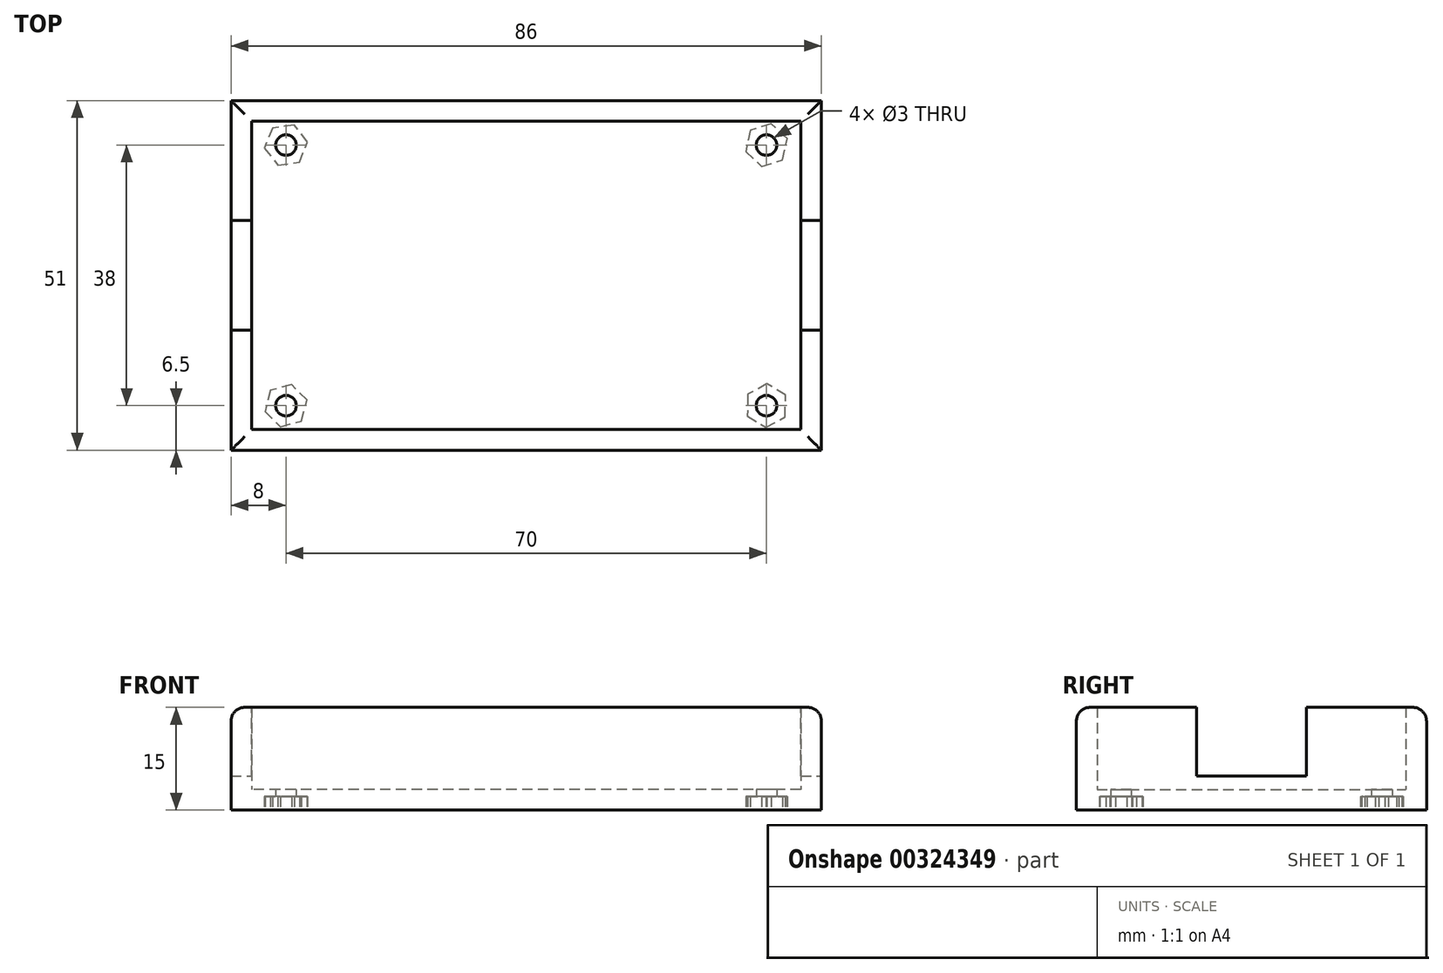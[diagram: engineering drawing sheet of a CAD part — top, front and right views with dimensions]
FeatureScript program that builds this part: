
annotation { "Feature Type Name" : "Feature", "Feature Type Description" : "" }
export const myFeature = defineFeature(function(context is Context, id is Id, definition is map)
    precondition{}
    {
        {
            var Q0;
            Q0=qCreatedBy(makeId("Top.planeOp"),FACE);
            var sketch = newSketch(context, id + "F0", { "sketchPlane" : qUnion([Q0])});
            skLineSegment(sketch, "E0.bottom", {"start": v(-40, 22.5) * mm, "end": v(40, 22.5) * mm});
            skLineSegment(sketch, "E0.top", {"start": v(-40, -22.5) * mm, "end": v(40, -22.5) * mm});
            skLineSegment(sketch, "E0.left", {"start": v(-40, 22.5) * mm, "end": v(-40, -22.5) * mm});
            skLineSegment(sketch, "E0.right", {"start": v(40, 22.5) * mm, "end": v(40, -22.5) * mm});
            skLineSegment(sketch, "E1.0", {"start": v(-43, 25.5) * mm, "end": v(43, 25.5) * mm});
            skLineSegment(sketch, "E1.1", {"start": v(-43, 25.5) * mm, "end": v(-43, -25.5) * mm});
            skLineSegment(sketch, "E1.2", {"start": v(-43, -25.5) * mm, "end": v(43, -25.5) * mm});
            skLineSegment(sketch, "E1.3", {"start": v(43, 25.5) * mm, "end": v(43, -25.5) * mm});
            skCircle(sketch, "E2", {"center": v(-35, 19) * mm, "radius": 1.5 * mm});
            skCircle(sketch, "E3", {"center": v(-35, -19) * mm, "radius": 1.5 * mm});
            skCircle(sketch, "E4", {"center": v(35, -19) * mm, "radius": 1.5 * mm});
            skCircle(sketch, "E5", {"center": v(35, 19) * mm, "radius": 1.5 * mm});
            skSolve(sketch);
        }
        {
            var Q0;
            Q0=makeQuery(id+"F0.imprint","IMPRINT",FACE,{"disambiguationData":[TD([[makeQuery(id+"F0.imprint","IMPRINT",EDGE,{"derivedFrom":sQuery(id+"F0.wireOp",EDGE,"E0.bottom")}),-1.0]])]});
            var Q1;
            Q1=makeQuery(id+"F0.imprint","IMPRINT",FACE,{"disambiguationData":[TD([[makeQuery(id+"F0.imprint","IMPRINT",EDGE,{"derivedFrom":sQuery(id+"F0.wireOp",EDGE,"E0.bottom")}),1.0]])]});
            extrude(context, id + "F1", {"entities" : qUnion([Q0, Q1]), "depth" : 3 * mm});
        }
        {
            var Q0;
            Q0=makeQuery(id+"F0.imprint","IMPRINT",FACE,{"disambiguationData":[TD([[makeQuery(id+"F0.imprint","IMPRINT",EDGE,{"derivedFrom":sQuery(id+"F0.wireOp",EDGE,"E0.bottom")}),1.0]])]});
            extrude(context, id + "F2", {"entities" : qUnion([Q0]), "operationType" : NewBodyOperationType.ADD, "depth" : 15 * mm});
        }
        {
            var Q0;
            Q0=makeQuery(id+"F2.opExtrude","CAP_FACE",FACE,{"disambiguationData":[OSD([sQuery(id+"F0.wireOp",EDGE,"E0.bottom"),sQuery(id+"F0.wireOp",EDGE,"E0.top"),sQuery(id+"F0.wireOp",EDGE,"E0.left"),sQuery(id+"F0.wireOp",EDGE,"E0.right"),sQuery(id+"F0.wireOp",EDGE,"E1.0"),sQuery(id+"F0.wireOp",EDGE,"E1.1"),sQuery(id+"F0.wireOp",EDGE,"E1.2"),sQuery(id+"F0.wireOp",EDGE,"E1.3")])],"isStart":false});
            var sketch = newSketch(context, id + "F3", { "sketchPlane" : qUnion([Q0])});
            skLineSegment(sketch, "E6.bottom", {"start": v(-43, 8) * mm, "end": v(-40, 8) * mm});
            skLineSegment(sketch, "E6.top", {"start": v(-43, -8) * mm, "end": v(-40, -8) * mm});
            skLineSegment(sketch, "E6.left", {"start": v(-43, 8) * mm, "end": v(-43, -8) * mm});
            skLineSegment(sketch, "E6.right", {"start": v(-40, 8) * mm, "end": v(-40, -8) * mm});
            skLineSegment(sketch, "E7.bottom", {"start": v(40, 8) * mm, "end": v(43, 8) * mm});
            skLineSegment(sketch, "E7.top", {"start": v(40, -8) * mm, "end": v(43, -8) * mm});
            skLineSegment(sketch, "E7.left", {"start": v(40, 8) * mm, "end": v(40, -8) * mm});
            skLineSegment(sketch, "E7.right", {"start": v(43, 8) * mm, "end": v(43, -8) * mm});
            skSolve(sketch);
        }
        {
            var Q0;
            Q0=makeQuery(id+"F3.imprint","IMPRINT",FACE,{"disambiguationData":[TD([[makeQuery(id+"F3.imprint","IMPRINT",EDGE,{"derivedFrom":sQuery(id+"F3.wireOp",EDGE,"E6.bottom")}),-1.0]])]});
            var Q1;
            Q1=makeQuery(id+"F3.imprint","IMPRINT",FACE,{"disambiguationData":[TD([[makeQuery(id+"F3.imprint","IMPRINT",EDGE,{"derivedFrom":sQuery(id+"F3.wireOp",EDGE,"E7.bottom")}),-1.0]])]});
            extrude(context, id + "F4", {"entities" : qUnion([Q0, Q1]), "operationType" : NewBodyOperationType.REMOVE, "oppositeDirection" : true, "depth" : 10 * mm});
        }
        {
            var Q0;
            Q0=makeQuery(id+"F0.imprint","IMPRINT",FACE,{"disambiguationData":[TD([[makeQuery(id+"F0.imprint","IMPRINT",EDGE,{"derivedFrom":sQuery(id+"F0.wireOp",EDGE,"E0.bottom")}),1.0]])]});
            var sketch = newSketch(context, id + "F5", { "sketchPlane" : qUnion([Q0])});
            skLineSegment(sketch, "E8.bottom", {"start": v(43, 25.5) * mm, "end": v(33, 25.5) * mm});
            skLineSegment(sketch, "E8.top", {"start": v(43, 15.5) * mm, "end": v(40, 15.5) * mm});
            skLineSegment(sketch, "E8.left", {"start": v(43, 25.5) * mm, "end": v(43, 15.5) * mm});
            skLineSegment(sketch, "E8.right", {"start": v(33, 25.5) * mm, "end": v(33, 22.5) * mm});
            skLineSegment(sketch, "E9.top", {"start": v(40, 22.5) * mm, "end": v(33, 22.5) * mm});
            skLineSegment(sketch, "E9.left", {"start": v(40, 15.5) * mm, "end": v(40, 22.5) * mm});
            skLineSegment(sketch, "E10.MirrorCS", {"start": v(-33, 25.5) * mm, "end": v(-33, 22.5) * mm});
            skLineSegment(sketch, "E11.MirrorCS", {"start": v(-40, 22.5) * mm, "end": v(-33, 22.5) * mm});
            skLineSegment(sketch, "E12.MirrorCS", {"start": v(-40, 15.5) * mm, "end": v(-40, 22.5) * mm});
            skLineSegment(sketch, "E13.MirrorCS", {"start": v(-43, 15.5) * mm, "end": v(-40, 15.5) * mm});
            skLineSegment(sketch, "E14.MirrorCS", {"start": v(-43, 25.5) * mm, "end": v(-43, 15.5) * mm});
            skLineSegment(sketch, "E15.MirrorCS", {"start": v(-43, 25.5) * mm, "end": v(-33, 25.5) * mm});
            skLineSegment(sketch, "E16.MirrorCS", {"start": v(43, -15.5) * mm, "end": v(40, -15.5) * mm});
            skLineSegment(sketch, "E17.MirrorCS", {"start": v(43, -25.5) * mm, "end": v(43, -15.5) * mm});
            skLineSegment(sketch, "E18.MirrorCS", {"start": v(40, -15.5) * mm, "end": v(40, -22.5) * mm});
            skLineSegment(sketch, "E19.MirrorCS", {"start": v(40, -22.5) * mm, "end": v(33, -22.5) * mm});
            skLineSegment(sketch, "E20.MirrorCS", {"start": v(33, -25.5) * mm, "end": v(33, -22.5) * mm});
            skLineSegment(sketch, "E21.MirrorCS", {"start": v(43, -25.5) * mm, "end": v(33, -25.5) * mm});
            skLineSegment(sketch, "E22.MirrorCS", {"start": v(-40, -22.5) * mm, "end": v(-33, -22.5) * mm});
            skLineSegment(sketch, "E23.MirrorCS", {"start": v(-33, -25.5) * mm, "end": v(-33, -22.5) * mm});
            skLineSegment(sketch, "E24.MirrorCS", {"start": v(-43, -25.5) * mm, "end": v(-33, -25.5) * mm});
            skLineSegment(sketch, "E25.MirrorCS", {"start": v(-43, -25.5) * mm, "end": v(-43, -15.5) * mm});
            skLineSegment(sketch, "E26.MirrorCS", {"start": v(-43, -15.5) * mm, "end": v(-40, -15.5) * mm});
            skLineSegment(sketch, "E27.MirrorCS", {"start": v(-40, -15.5) * mm, "end": v(-40, -22.5) * mm});
            skSolve(sketch);
        }
        {
            var Q0;
            Q0=makeQuery(id+"F1.opExtrude","CAP_FACE",FACE,{"disambiguationData":[OSD([sQuery(id+"F0.wireOp",EDGE,"E1.0"),sQuery(id+"F0.wireOp",EDGE,"E1.1"),sQuery(id+"F0.wireOp",EDGE,"E1.2"),sQuery(id+"F0.wireOp",EDGE,"E1.3"),sQuery(id+"F0.wireOp",EDGE,"E2"),sQuery(id+"F0.wireOp",EDGE,"E3"),sQuery(id+"F0.wireOp",EDGE,"E4"),sQuery(id+"F0.wireOp",EDGE,"E5")])],"isStart":true});
            var sketch = newSketch(context, id + "F6", { "sketchPlane" : qUnion([Q0])});
            skCircle(sketch, "E28.cCircle", {"center": v(-35, 19) * mm, "radius": 2.75 * mm, "construction": true});
            skLineSegment(sketch, "E28.0", {"start": v(-31.94, 18.16) * mm, "end": v(-34.2, 15.93) * mm});
            skLineSegment(sketch, "E28.1", {"start": v(-34.2, 15.93) * mm, "end": v(-37.26, 16.77) * mm});
            skLineSegment(sketch, "E28.2", {"start": v(-37.26, 16.77) * mm, "end": v(-38.06, 19.84) * mm});
            skLineSegment(sketch, "E28.3", {"start": v(-38.06, 19.84) * mm, "end": v(-35.8, 22.07) * mm});
            skLineSegment(sketch, "E28.4", {"start": v(-35.8, 22.07) * mm, "end": v(-32.74, 21.23) * mm});
            skLineSegment(sketch, "E28.5", {"start": v(-32.74, 21.23) * mm, "end": v(-31.94, 18.16) * mm});
            skPoint(sketch, "E28.0.midPoint", {"position": v(-33.07, 17.05) * mm});
            skCircle(sketch, "E29.cCircle", {"center": v(35, 19) * mm, "radius": 2.75 * mm, "construction": true});
            skLineSegment(sketch, "E29.0", {"start": v(37.78, 17.47) * mm, "end": v(35.07, 15.83) * mm});
            skLineSegment(sketch, "E29.1", {"start": v(35.07, 15.83) * mm, "end": v(32.29, 17.35) * mm});
            skLineSegment(sketch, "E29.2", {"start": v(32.29, 17.35) * mm, "end": v(32.22, 20.53) * mm});
            skLineSegment(sketch, "E29.3", {"start": v(32.22, 20.53) * mm, "end": v(34.93, 22.17) * mm});
            skLineSegment(sketch, "E29.4", {"start": v(34.93, 22.17) * mm, "end": v(37.71, 20.65) * mm});
            skLineSegment(sketch, "E29.5", {"start": v(37.71, 20.65) * mm, "end": v(37.78, 17.47) * mm});
            skPoint(sketch, "E29.0.midPoint", {"position": v(36.43, 16.65) * mm});
            skCircle(sketch, "E30.cCircle", {"center": v(-35, -19) * mm, "radius": 2.75 * mm, "construction": true});
            skLineSegment(sketch, "E30.0", {"start": v(-31.86, -19.44) * mm, "end": v(-33.81, -21.94) * mm});
            skLineSegment(sketch, "E30.1", {"start": v(-33.81, -21.94) * mm, "end": v(-36.96, -21.5) * mm});
            skLineSegment(sketch, "E30.2", {"start": v(-36.96, -21.5) * mm, "end": v(-38.14, -18.56) * mm});
            skLineSegment(sketch, "E30.3", {"start": v(-38.14, -18.56) * mm, "end": v(-36.19, -16.06) * mm});
            skLineSegment(sketch, "E30.4", {"start": v(-36.19, -16.06) * mm, "end": v(-33.04, -16.5) * mm});
            skLineSegment(sketch, "E30.5", {"start": v(-33.04, -16.5) * mm, "end": v(-31.86, -19.44) * mm});
            skPoint(sketch, "E30.0.midPoint", {"position": v(-32.83, -20.7) * mm});
            skCircle(sketch, "E31.cCircle", {"center": v(35, -19) * mm, "radius": 2.75 * mm, "construction": true});
            skLineSegment(sketch, "E31.0", {"start": v(38.03, -19.96) * mm, "end": v(35.68, -22.1) * mm});
            skLineSegment(sketch, "E31.1", {"start": v(35.68, -22.1) * mm, "end": v(32.65, -21.14) * mm});
            skLineSegment(sketch, "E31.2", {"start": v(32.65, -21.14) * mm, "end": v(31.97, -18.04) * mm});
            skLineSegment(sketch, "E31.3", {"start": v(31.97, -18.04) * mm, "end": v(34.32, -15.9) * mm});
            skLineSegment(sketch, "E31.4", {"start": v(34.32, -15.9) * mm, "end": v(37.35, -16.86) * mm});
            skLineSegment(sketch, "E31.5", {"start": v(37.35, -16.86) * mm, "end": v(38.03, -19.96) * mm});
            skPoint(sketch, "E31.0.midPoint", {"position": v(36.85, -21.03) * mm});
            skSolve(sketch);
        }
        {
            var Q0;
            Q0=makeQuery(id+"F6.imprint","IMPRINT",FACE,{"disambiguationData":[TD([[makeQuery(id+"F6.imprint","IMPRINT",EDGE,{"derivedFrom":sQuery(id+"F6.wireOp",EDGE,"E28.0")}),-1.0]])]});
            var Q1;
            Q1=makeQuery(id+"F6.imprint","IMPRINT",FACE,{"disambiguationData":[TD([[makeQuery(id+"F6.imprint","IMPRINT",EDGE,{"derivedFrom":sQuery(id+"F6.wireOp",EDGE,"E30.0")}),-1.0]])]});
            var Q2;
            Q2=makeQuery(id+"F6.imprint","IMPRINT",FACE,{"disambiguationData":[TD([[makeQuery(id+"F6.imprint","IMPRINT",EDGE,{"derivedFrom":sQuery(id+"F6.wireOp",EDGE,"E31.0")}),-1.0]])]});
            var Q3;
            Q3=makeQuery(id+"F6.imprint","IMPRINT",FACE,{"disambiguationData":[TD([[makeQuery(id+"F6.imprint","IMPRINT",EDGE,{"derivedFrom":sQuery(id+"F6.wireOp",EDGE,"E29.0")}),-1.0]])]});
            extrude(context, id + "F7", {"entities" : qUnion([Q0, Q1, Q2, Q3]), "operationType" : NewBodyOperationType.REMOVE, "oppositeDirection" : true, "depth" : 2 * mm});
        }
        {
            var Q0;
            Q0=makeQuery(id+"F2.opExtrude","CAP_EDGE",EDGE,{"disambiguationData":[OSD([sQuery(id+"F0.wireOp",EDGE,"E1.2")])],"isStart":false});
            var Q1;
            Q1=makeQuery(id+"F2.opExtrude","CAP_EDGE",EDGE,{"disambiguationData":[OSD([sQuery(id+"F0.wireOp",EDGE,"E1.0")])],"isStart":false});
            var Q2;
            {var subQ0=sQuery(id+"F0.wireOp",EDGE,"E1.0");var subQ1=sQuery(id+"F0.wireOp",EDGE,"E1.3");Q2=makeQuery(id+"F4.boolean.opBoolean","SPLIT",EDGE,{"disambiguationData":[TD([makeQuery(id+"F1.opExtrude","SWEPT_FACE",FACE,{"disambiguationData":[OSD([subQ0])]})])],"derivedFrom":makeQuery(id+"F2.opExtrude","CAP_EDGE",EDGE,{"disambiguationData":[OSD([subQ1])],"isStart":false})});}
            var Q3;
            {var subQ0=sQuery(id+"F0.wireOp",EDGE,"E1.3");var subQ1=sQuery(id+"F0.wireOp",EDGE,"E1.2");Q3=makeQuery(id+"F4.boolean.opBoolean","SPLIT",EDGE,{"disambiguationData":[TD([makeQuery(id+"F1.opExtrude","SWEPT_FACE",FACE,{"disambiguationData":[OSD([subQ1])]})])],"derivedFrom":makeQuery(id+"F2.opExtrude","CAP_EDGE",EDGE,{"disambiguationData":[OSD([subQ0])],"isStart":false})});}
            var Q4;
            {var subQ0=sQuery(id+"F0.wireOp",EDGE,"E1.0");var subQ1=sQuery(id+"F0.wireOp",EDGE,"E1.1");Q4=makeQuery(id+"F4.boolean.opBoolean","SPLIT",EDGE,{"disambiguationData":[TD([makeQuery(id+"F1.opExtrude","SWEPT_FACE",FACE,{"disambiguationData":[OSD([subQ0])]})])],"derivedFrom":makeQuery(id+"F2.opExtrude","CAP_EDGE",EDGE,{"disambiguationData":[OSD([subQ1])],"isStart":false})});}
            var Q5;
            {var subQ0=sQuery(id+"F0.wireOp",EDGE,"E1.2");var subQ1=sQuery(id+"F0.wireOp",EDGE,"E1.1");Q5=makeQuery(id+"F4.boolean.opBoolean","SPLIT",EDGE,{"disambiguationData":[TD([makeQuery(id+"F1.opExtrude","SWEPT_FACE",FACE,{"disambiguationData":[OSD([subQ0])]})])],"derivedFrom":makeQuery(id+"F2.opExtrude","CAP_EDGE",EDGE,{"disambiguationData":[OSD([subQ1])],"isStart":false})});}
            fillet(context, id + "F8", {"entities" : qUnion([Q0, Q1, Q2, Q3, Q4, Q5]), "radius" : 2 * mm, "tangentPropagation" : true, "allowEdgeOverflow" : false});
        }
    });
